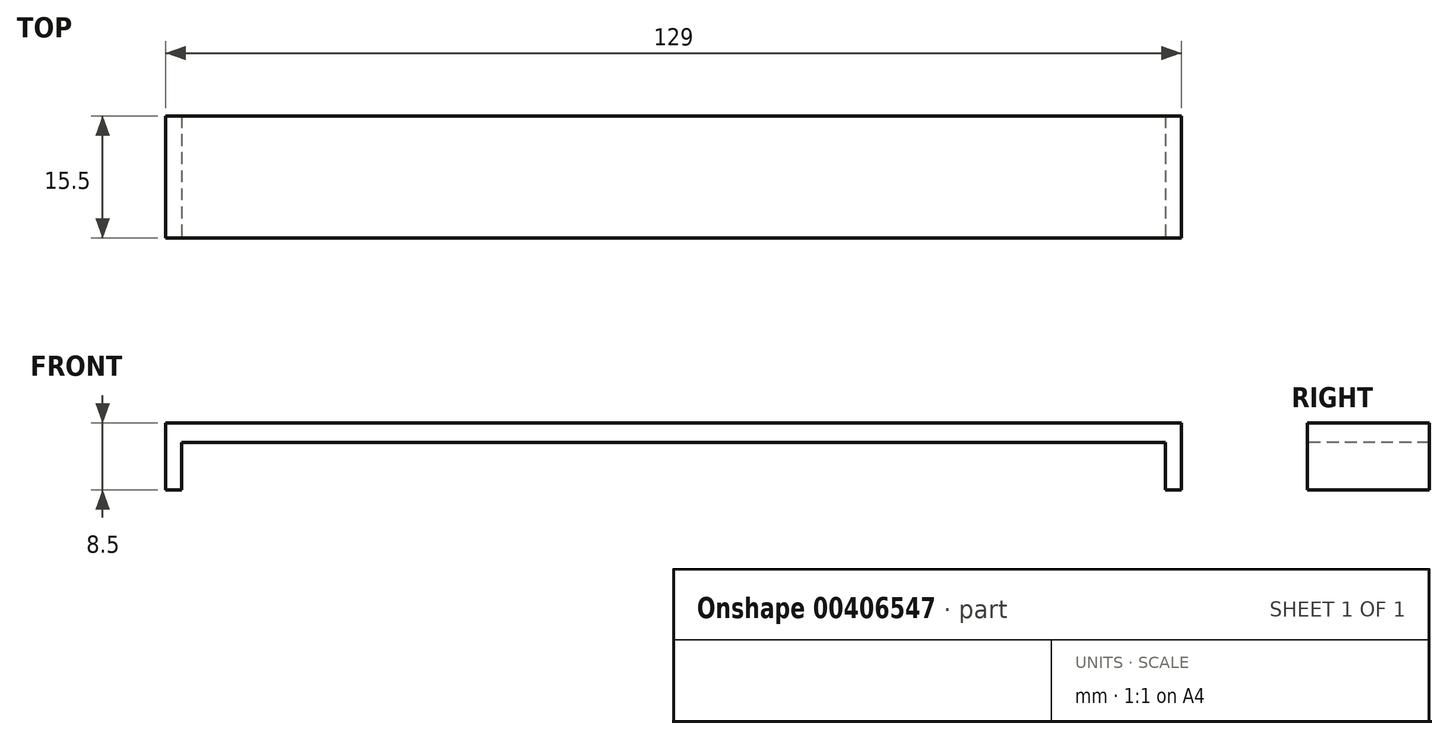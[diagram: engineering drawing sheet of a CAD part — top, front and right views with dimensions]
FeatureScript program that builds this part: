
annotation { "Feature Type Name" : "Feature", "Feature Type Description" : "" }
export const myFeature = defineFeature(function(context is Context, id is Id, definition is map)
    precondition{}
    {
        {
            var Q0;
            Q0=qCreatedBy(makeId("Top.planeOp"),FACE);
            var sketch = newSketch(context, id + "F0", { "sketchPlane" : qUnion([Q0])});
            skLineSegment(sketch, "E0.bottom", {"start": v(64.5, 7.75) * mm, "end": v(-64.5, 7.75) * mm});
            skLineSegment(sketch, "E0.top", {"start": v(64.5, -7.75) * mm, "end": v(-64.5, -7.75) * mm});
            skLineSegment(sketch, "E0.left", {"start": v(64.5, 7.75) * mm, "end": v(64.5, -7.75) * mm});
            skLineSegment(sketch, "E0.right", {"start": v(-64.5, 7.75) * mm, "end": v(-64.5, -7.75) * mm});
            skPoint(sketch, "E0.middle", {"position": v(0, 0) * mm});
            skLineSegment(sketch, "E1.0", {"start": v(-62.5, 7.75) * mm, "end": v(-62.5, -7.75) * mm});
            skLineSegment(sketch, "E2.0", {"start": v(62.5, 7.75) * mm, "end": v(62.5, -7.75) * mm});
            skSolve(sketch);
        }
        {
            var Q0;
            Q0 = qSketchRegion(id + "F0", true);
            extrude(context, id + "F1", {"entities" : qUnion([Q0]), "depth" : 2.5 * mm});
        }
        {
            var Q0;
            {var subQ0=sQuery(id+"F0.wireOp",EDGE,"E0.right");Q0=makeQuery(id+"F0.imprint","IMPRINT",FACE,{"disambiguationData":[TD([[makeQuery(id+"F0.imprint","IMPRINT",EDGE,{"derivedFrom":subQ0}),1.0]])]});}
            var Q1;
            {var subQ0=sQuery(id+"F0.wireOp",EDGE,"E0.left");Q1=makeQuery(id+"F0.imprint","IMPRINT",FACE,{"disambiguationData":[TD([[makeQuery(id+"F0.imprint","IMPRINT",EDGE,{"derivedFrom":subQ0}),-1.0]])]});}
            extrude(context, id + "F2", {"entities" : qUnion([Q0, Q1]), "operationType" : NewBodyOperationType.ADD, "oppositeDirection" : true, "depth" : 6 * mm});
        }
    });
